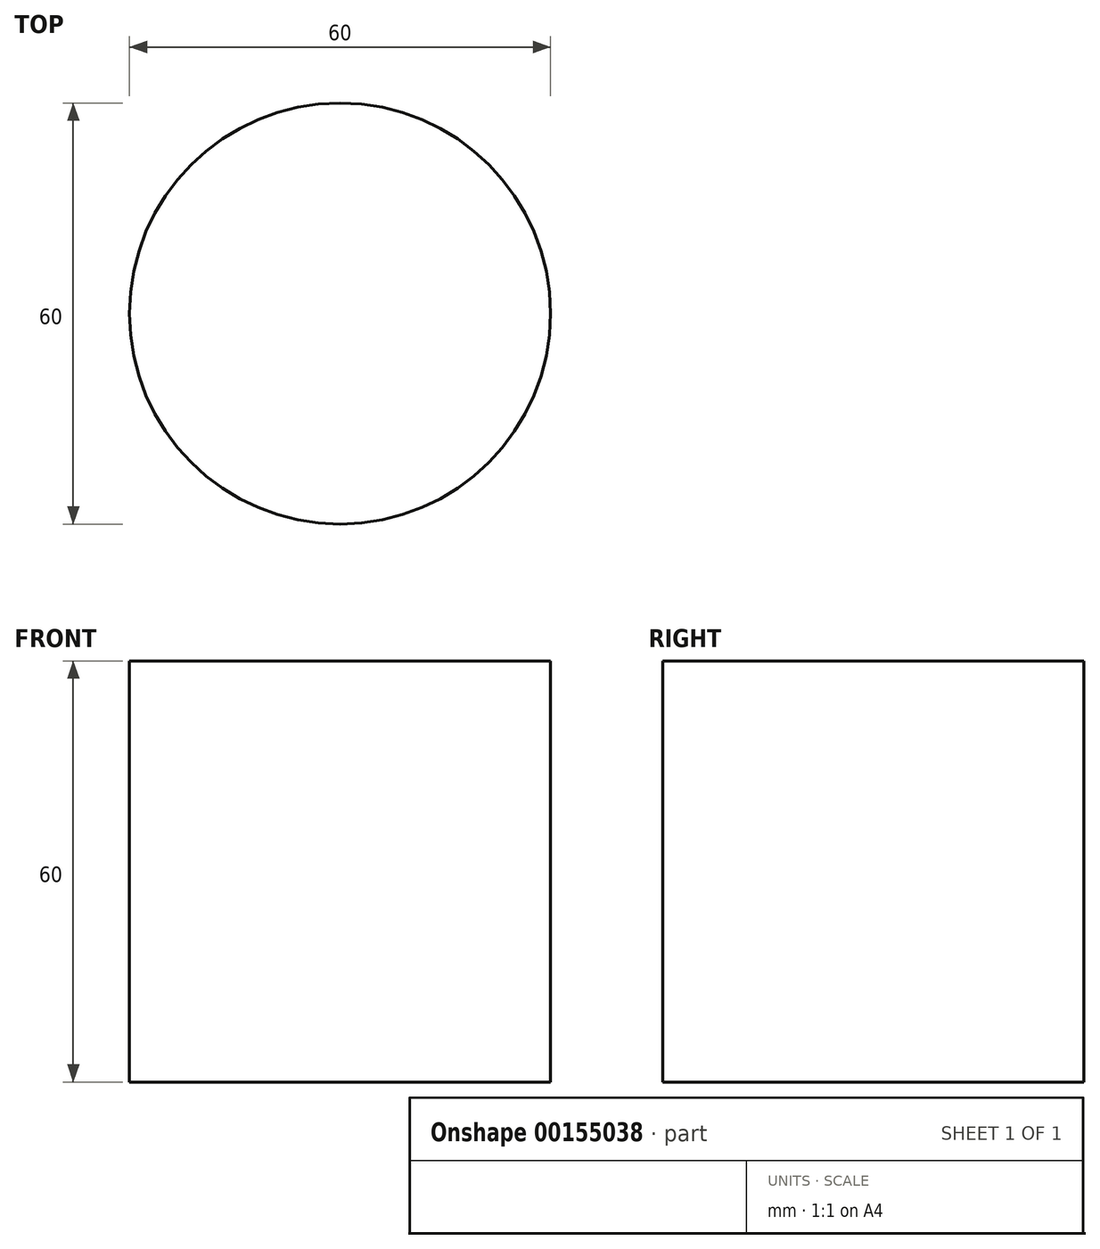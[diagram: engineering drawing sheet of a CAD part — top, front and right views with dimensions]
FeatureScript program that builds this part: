
annotation { "Feature Type Name" : "Feature", "Feature Type Description" : "" }
export const myFeature = defineFeature(function(context is Context, id is Id, definition is map)
    precondition{}
    {
        {
            var Q0;
            Q0=qCreatedBy(makeId("Top.planeOp"),FACE);
            var sketch = newSketch(context, id + "F0", { "sketchPlane" : qUnion([Q0])});
            skCircle(sketch, "E0", {"center": v(0, 0) * mm, "radius": 30 * mm});
            skSolve(sketch);
        }
        {
            var Q0;
            Q0=makeQuery(id+"F0.imprint","IMPRINT",FACE,{"disambiguationData":[TD([[makeQuery(id+"F0.imprint","IMPRINT",EDGE,{"derivedFrom":sQuery(id+"F0.wireOp",EDGE,"E0")}),1.0]])]});
            extrude(context, id + "F1", {"entities" : qUnion([Q0]), "depth" : 60 * mm});
        }
    });
